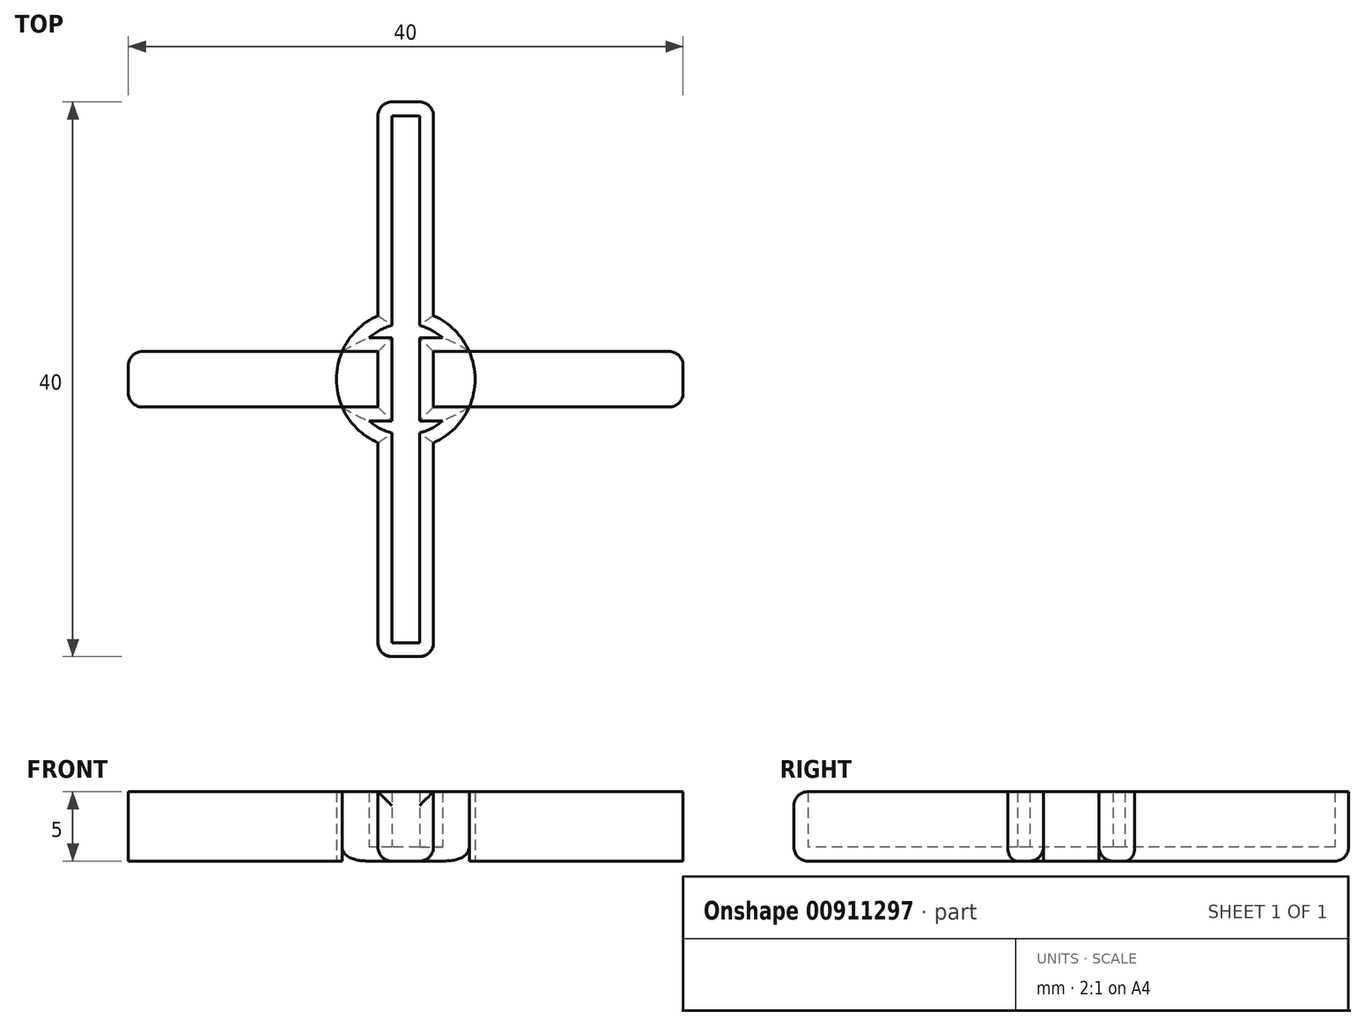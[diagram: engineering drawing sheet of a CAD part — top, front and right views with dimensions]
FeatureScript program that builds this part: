
annotation { "Feature Type Name" : "Feature", "Feature Type Description" : "" }
export const myFeature = defineFeature(function(context is Context, id is Id, definition is map)
    precondition{}
    {
        {
            var Q0;
            Q0=qCreatedBy(makeId("Top.planeOp"),FACE);
            var sketch = newSketch(context, id + "F0", { "sketchPlane" : qUnion([Q0])});
            skCircle(sketch, "E0", {"center": v(0, 0) * mm, "radius": 5 * mm});
            skLineSegment(sketch, "E1.bottom", {"start": v(20, -2) * mm, "end": v(-20, -2) * mm});
            skLineSegment(sketch, "E1.top", {"start": v(20, 2) * mm, "end": v(-20, 2) * mm});
            skLineSegment(sketch, "E1.left", {"start": v(20, -2) * mm, "end": v(20, 2) * mm});
            skLineSegment(sketch, "E1.right", {"start": v(-20, -2) * mm, "end": v(-20, 2) * mm});
            skLineSegment(sketch, "E2.bottom", {"start": v(2, 20) * mm, "end": v(-2, 20) * mm});
            skLineSegment(sketch, "E2.top", {"start": v(2, -20) * mm, "end": v(-2, -20) * mm});
            skLineSegment(sketch, "E2.left", {"start": v(2, 20) * mm, "end": v(2, -20) * mm});
            skLineSegment(sketch, "E2.right", {"start": v(-2, 20) * mm, "end": v(-2, -20) * mm});
            skSolve(sketch);
        }
        {
            var Q0;
            {var subQ5=sQuery(id+"F0.wireOp",EDGE,"E2.bottom");Q0=makeQuery(id+"F0.imprint","IMPRINT",FACE,{"disambiguationData":[TD([[makeQuery(id+"F0.imprint","IMPRINT",EDGE,{"derivedFrom":subQ5}),1.0]])]});}
            var Q1;
            {var subQ0=sQuery(id+"F0.wireOp",EDGE,"E2.left");var subQ1=sQuery(id+"F0.wireOp",EDGE,"E0");var subQ2=makeQuery(id+"F0.imprint","INTERSECT",VERTEX,{"disambiguationData":[OD(0.0)],"derivedFrom":[subQ1,subQ0]});Q1=makeQuery(id+"F0.imprint","IMPRINT",FACE,{"disambiguationData":[TD([[makeQuery(id+"F0.imprint","IMPRINT",EDGE,{"disambiguationData":[TD([[subQ2,-1.0]])],"derivedFrom":subQ1}),1.0]])]});}
            var Q2;
            {var subQ0=sQuery(id+"F0.wireOp",EDGE,"E2.left");var subQ1=sQuery(id+"F0.wireOp",EDGE,"E1.bottom");var subQ2=makeQuery(id+"F0.imprint","INTERSECT",VERTEX,{"derivedFrom":[subQ1,subQ0]});Q2=makeQuery(id+"F0.imprint","IMPRINT",FACE,{"disambiguationData":[TD([[makeQuery(id+"F0.imprint","IMPRINT",EDGE,{"disambiguationData":[TD([[subQ2,-1.0]])],"derivedFrom":subQ1}),-1.0]])]});}
            var Q3;
            {var subQ0=sQuery(id+"F0.wireOp",EDGE,"E2.right");var subQ1=sQuery(id+"F0.wireOp",EDGE,"E0");var subQ2=makeQuery(id+"F0.imprint","INTERSECT",VERTEX,{"disambiguationData":[OD(1.0)],"derivedFrom":[subQ1,subQ0]});Q3=makeQuery(id+"F0.imprint","IMPRINT",FACE,{"disambiguationData":[TD([[makeQuery(id+"F0.imprint","IMPRINT",EDGE,{"disambiguationData":[TD([[subQ2,-1.0]])],"derivedFrom":subQ1}),1.0]])]});}
            var Q4;
            {var subQ5=sQuery(id+"F0.wireOp",EDGE,"E2.top");Q4=makeQuery(id+"F0.imprint","IMPRINT",FACE,{"disambiguationData":[TD([[makeQuery(id+"F0.imprint","IMPRINT",EDGE,{"derivedFrom":subQ5}),-1.0]])]});}
            var Q5;
            {var subQ5=sQuery(id+"F0.wireOp",EDGE,"E1.left");Q5=makeQuery(id+"F0.imprint","IMPRINT",FACE,{"disambiguationData":[TD([[makeQuery(id+"F0.imprint","IMPRINT",EDGE,{"derivedFrom":subQ5}),1.0]])]});}
            var Q6;
            {var subQ0=sQuery(id+"F0.wireOp",EDGE,"E2.left");var subQ1=sQuery(id+"F0.wireOp",EDGE,"E0");var subQ2=makeQuery(id+"F0.imprint","INTERSECT",VERTEX,{"disambiguationData":[OD(0.0)],"derivedFrom":[subQ1,subQ0]});Q6=makeQuery(id+"F0.imprint","IMPRINT",FACE,{"disambiguationData":[TD([[makeQuery(id+"F0.imprint","IMPRINT",EDGE,{"disambiguationData":[TD([[subQ2,1.0]])],"derivedFrom":subQ1}),1.0]])]});}
            var Q7;
            {var subQ0=sQuery(id+"F0.wireOp",EDGE,"E1.top");var subQ1=sQuery(id+"F0.wireOp",EDGE,"E0");var subQ2=makeQuery(id+"F0.imprint","INTERSECT",VERTEX,{"disambiguationData":[OD(0.0)],"derivedFrom":[subQ1,subQ0]});Q7=makeQuery(id+"F0.imprint","IMPRINT",FACE,{"disambiguationData":[TD([[makeQuery(id+"F0.imprint","IMPRINT",EDGE,{"disambiguationData":[TD([[subQ2,1.0]])],"derivedFrom":subQ1}),1.0]])]});}
            var Q8;
            {var subQ0=sQuery(id+"F0.wireOp",EDGE,"E2.left");var subQ1=sQuery(id+"F0.wireOp",EDGE,"E0");var subQ2=makeQuery(id+"F0.imprint","INTERSECT",VERTEX,{"disambiguationData":[OD(1.0)],"derivedFrom":[subQ1,subQ0]});Q8=makeQuery(id+"F0.imprint","IMPRINT",FACE,{"disambiguationData":[TD([[makeQuery(id+"F0.imprint","IMPRINT",EDGE,{"disambiguationData":[TD([[subQ2,-1.0]])],"derivedFrom":subQ1}),1.0]])]});}
            var Q9;
            {var subQ0=sQuery(id+"F0.wireOp",EDGE,"E1.top");var subQ1=sQuery(id+"F0.wireOp",EDGE,"E0");var subQ2=makeQuery(id+"F0.imprint","INTERSECT",VERTEX,{"disambiguationData":[OD(1.0)],"derivedFrom":[subQ1,subQ0]});Q9=makeQuery(id+"F0.imprint","IMPRINT",FACE,{"disambiguationData":[TD([[makeQuery(id+"F0.imprint","IMPRINT",EDGE,{"disambiguationData":[TD([[subQ2,-1.0]])],"derivedFrom":subQ1}),1.0]])]});}
            var Q10;
            {var subQ0=sQuery(id+"F0.wireOp",EDGE,"E2.right");var subQ1=sQuery(id+"F0.wireOp",EDGE,"E0");var subQ2=makeQuery(id+"F0.imprint","INTERSECT",VERTEX,{"disambiguationData":[OD(0.0)],"derivedFrom":[subQ1,subQ0]});Q10=makeQuery(id+"F0.imprint","IMPRINT",FACE,{"disambiguationData":[TD([[makeQuery(id+"F0.imprint","IMPRINT",EDGE,{"disambiguationData":[TD([[subQ2,-1.0]])],"derivedFrom":subQ1}),1.0]])]});}
            var Q11;
            {var subQ0=sQuery(id+"F0.wireOp",EDGE,"E1.bottom");var subQ1=sQuery(id+"F0.wireOp",EDGE,"E0");var subQ2=makeQuery(id+"F0.imprint","INTERSECT",VERTEX,{"disambiguationData":[OD(0.0)],"derivedFrom":[subQ1,subQ0]});Q11=makeQuery(id+"F0.imprint","IMPRINT",FACE,{"disambiguationData":[TD([[makeQuery(id+"F0.imprint","IMPRINT",EDGE,{"disambiguationData":[TD([[subQ2,-1.0]])],"derivedFrom":subQ1}),1.0]])]});}
            var Q12;
            {var subQ5=sQuery(id+"F0.wireOp",EDGE,"E1.right");Q12=makeQuery(id+"F0.imprint","IMPRINT",FACE,{"disambiguationData":[TD([[makeQuery(id+"F0.imprint","IMPRINT",EDGE,{"derivedFrom":subQ5}),-1.0]])]});}
            extrude(context, id + "F1", {"entities" : qUnion([Q0, Q1, Q2, Q3, Q4, Q5, Q6, Q7, Q8, Q9, Q10, Q11, Q12]), "depth" : 5 * mm, "offsetDistance" : 25 * mm});
        }
        {
            var Q0;
            Q0=makeQuery(id+"F1.opExtrude","CAP_FACE",FACE,{"disambiguationData":[OSD([sQuery(id+"F0.wireOp",EDGE,"E0"),sQuery(id+"F0.wireOp",EDGE,"E1.bottom"),sQuery(id+"F0.wireOp",EDGE,"E1.top"),sQuery(id+"F0.wireOp",EDGE,"E1.left"),sQuery(id+"F0.wireOp",EDGE,"E1.right"),sQuery(id+"F0.wireOp",EDGE,"E2.bottom"),sQuery(id+"F0.wireOp",EDGE,"E2.top"),sQuery(id+"F0.wireOp",EDGE,"E2.left"),sQuery(id+"F0.wireOp",EDGE,"E2.right")])],"isStart":false});
            shell(context, id + "F2", {"entities" : qUnion([Q0]), "thickness" : 1 * mm});
        }
        {
            var Q0;
            Q0=makeQuery(id+"F1.opExtrude","CAP_FACE",FACE,{"disambiguationData":[OSD([sQuery(id+"F0.wireOp",EDGE,"E0"),sQuery(id+"F0.wireOp",EDGE,"E1.bottom"),sQuery(id+"F0.wireOp",EDGE,"E1.top"),sQuery(id+"F0.wireOp",EDGE,"E1.left"),sQuery(id+"F0.wireOp",EDGE,"E1.right"),sQuery(id+"F0.wireOp",EDGE,"E2.bottom"),sQuery(id+"F0.wireOp",EDGE,"E2.top"),sQuery(id+"F0.wireOp",EDGE,"E2.left"),sQuery(id+"F0.wireOp",EDGE,"E2.right")])],"isStart":true});
            var Q1;
            Q1=makeQuery(id+"F1.opExtrude","SWEPT_EDGE",EDGE,{"disambiguationData":[OSD([sQuery(id+"F0.wireOp",EDGE,"E2.top"),sQuery(id+"F0.wireOp",EDGE,"E2.left")])]});
            var Q2;
            Q2=makeQuery(id+"F1.opExtrude","SWEPT_FACE",FACE,{"disambiguationData":[OSD([sQuery(id+"F0.wireOp",EDGE,"E2.top")])]});
            var Q3;
            Q3=makeQuery(id+"F1.opExtrude","SWEPT_EDGE",EDGE,{"disambiguationData":[OSD([sQuery(id+"F0.wireOp",EDGE,"E1.top"),sQuery(id+"F0.wireOp",EDGE,"E1.right")])]});
            var Q4;
            Q4=makeQuery(id+"F1.opExtrude","SWEPT_EDGE",EDGE,{"disambiguationData":[OSD([sQuery(id+"F0.wireOp",EDGE,"E1.bottom"),sQuery(id+"F0.wireOp",EDGE,"E1.right")])]});
            var Q5;
            Q5=makeQuery(id+"F1.opExtrude","SWEPT_EDGE",EDGE,{"disambiguationData":[OSD([sQuery(id+"F0.wireOp",EDGE,"E2.bottom"),sQuery(id+"F0.wireOp",EDGE,"E2.right")])]});
            var Q6;
            Q6=makeQuery(id+"F1.opExtrude","SWEPT_EDGE",EDGE,{"disambiguationData":[OSD([sQuery(id+"F0.wireOp",EDGE,"E2.bottom"),sQuery(id+"F0.wireOp",EDGE,"E2.left")])]});
            var Q7;
            Q7=makeQuery(id+"F1.opExtrude","SWEPT_EDGE",EDGE,{"disambiguationData":[OSD([sQuery(id+"F0.wireOp",EDGE,"E1.top"),sQuery(id+"F0.wireOp",EDGE,"E1.left")])]});
            var Q8;
            Q8=makeQuery(id+"F1.opExtrude","SWEPT_EDGE",EDGE,{"disambiguationData":[OSD([sQuery(id+"F0.wireOp",EDGE,"E1.bottom"),sQuery(id+"F0.wireOp",EDGE,"E1.left")])]});
            fillet(context, id + "F3", {"entities" : qUnion([Q0, Q1, Q2, Q3, Q4, Q5, Q6, Q7, Q8]), "radius" : 1 * mm, "tangentPropagation" : true, "allowEdgeOverflow" : false});
        }
    });
